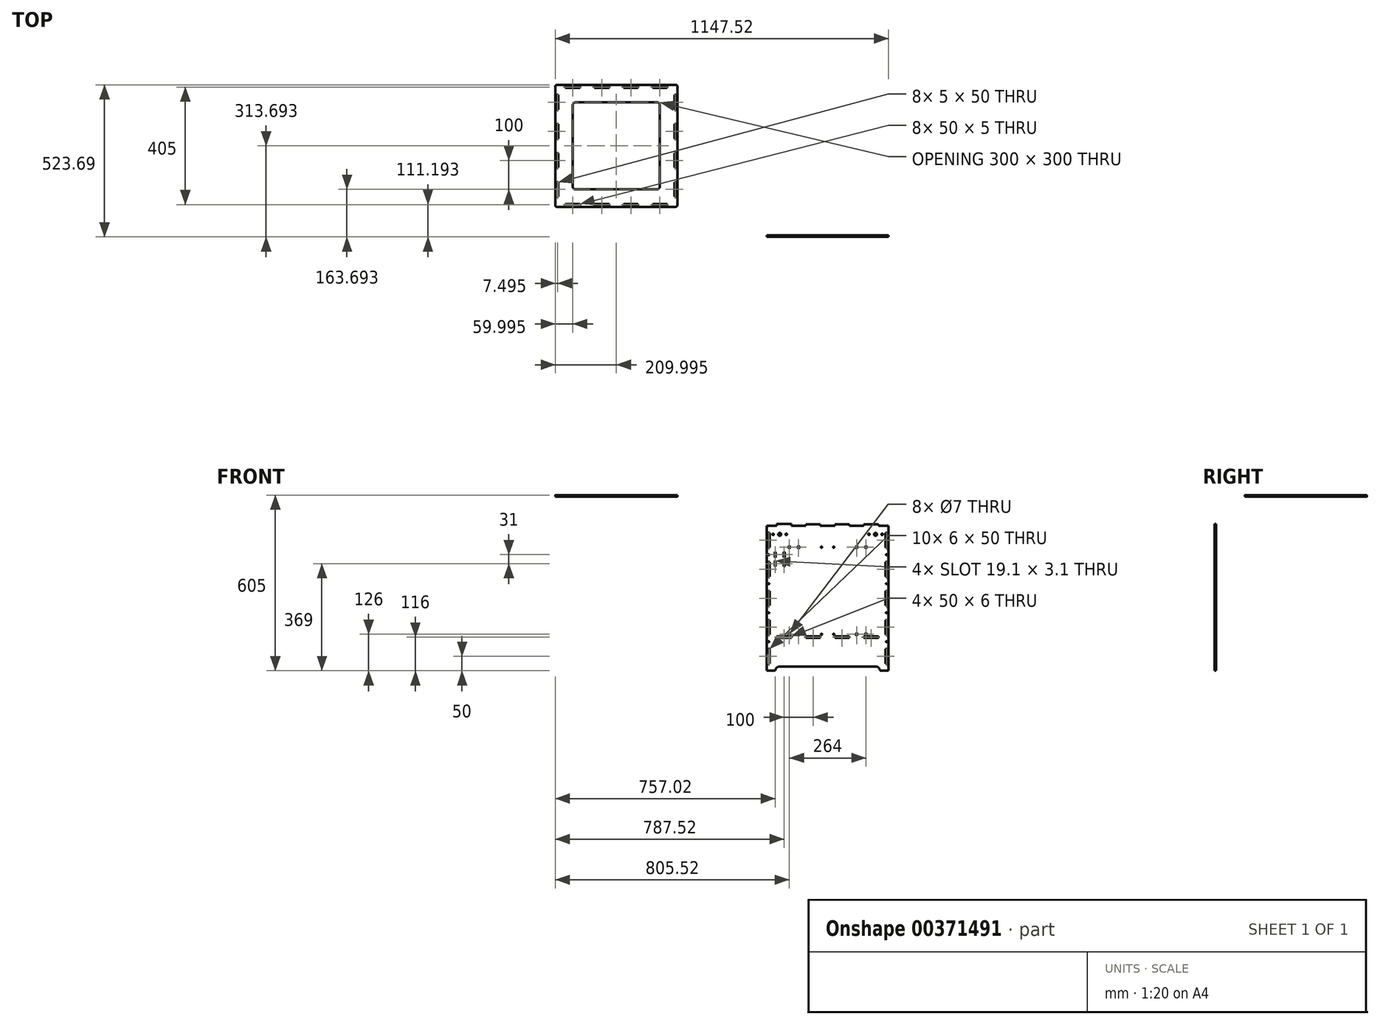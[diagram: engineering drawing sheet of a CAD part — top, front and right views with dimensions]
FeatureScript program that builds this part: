
annotation { "Feature Type Name" : "Feature", "Feature Type Description" : "" }
export const myFeature = defineFeature(function(context is Context, id is Id, definition is map)
    precondition{}
    {
        {
            var Q0;
            Q0=qCreatedBy(makeId("Front.planeOp"),FACE);
            var sketch = newSketch(context, id + "F0", { "sketchPlane" : qUnion([Q0])});
            skLineSegment(sketch, "E0.bottom", {"start": v(0, 0) * mm, "end": v(30, 0) * mm});
            skLineSegment(sketch, "E0.left", {"start": v(0, 0) * mm, "end": v(0, 500) * mm});
            skLineSegment(sketch, "E0.right", {"start": v(420, 0) * mm, "end": v(420, 500) * mm});
            skCircle(sketch, "E1", {"center": v(22.5, 470) * mm, "radius": 2.6 * mm});
            skCircle(sketch, "E2", {"center": v(67.5, 470) * mm, "radius": 2.6 * mm});
            skCircle(sketch, "E3", {"center": v(352.5, 470) * mm, "radius": 2.6 * mm});
            skCircle(sketch, "E4", {"center": v(397.5, 470) * mm, "radius": 2.6 * mm});
            skPoint(sketch, "E5.endSnap0", {"position": v(210, 0) * mm});
            skPoint(sketch, "E6.orphan", {"position": v(135, 0) * mm});
            skPoint(sketch, "E7.orphan", {"position": v(285, 0) * mm});
            skPoint(sketch, "E8", {"position": v(30, 0) * mm});
            skPoint(sketch, "E9", {"position": v(390, 0) * mm});
            skPoint(sketch, "E10", {"position": v(45, 0) * mm});
            skPoint(sketch, "E11", {"position": v(375, 0) * mm});
            skLineSegment(sketch, "E12.trimOffspring", {"start": v(390, 0) * mm, "end": v(420, 0) * mm});
            skLineSegment(sketch, "E13", {"start": v(375, 15) * mm, "end": v(45, 15) * mm});
            skArc(sketch, "E14", {"start": v(390, 0) * mm, "mid": v(385.6, 10.6) * mm, "end": v(375, 15) * mm});
            skArc(sketch, "E15", {"start": v(45, 15) * mm, "mid": v(34.4, 10.6) * mm, "end": v(30, 0) * mm});
            skCircle(sketch, "E16", {"center": v(45, 470) * mm, "radius": 5 * mm});
            skCircle(sketch, "E17", {"center": v(375, 470) * mm, "radius": 5 * mm});
            skCircle(sketch, "E18", {"center": v(231, 126) * mm, "radius": 2.1 * mm});
            skCircle(sketch, "E19", {"center": v(189, 126) * mm, "radius": 2.1 * mm});
            skCircle(sketch, "E20", {"center": v(231, 426) * mm, "radius": 2.1 * mm});
            skCircle(sketch, "E21", {"center": v(189, 426) * mm, "radius": 2.1 * mm});
            skCircle(sketch, "E22", {"center": v(342, 126) * mm, "radius": 3.5 * mm});
            skCircle(sketch, "E23", {"center": v(310, 126) * mm, "radius": 3.5 * mm});
            skCircle(sketch, "E24", {"center": v(342, 426) * mm, "radius": 3.5 * mm});
            skCircle(sketch, "E25", {"center": v(310, 426) * mm, "radius": 3.5 * mm});
            skCircle(sketch, "E26", {"center": v(110, 126) * mm, "radius": 3.5 * mm});
            skCircle(sketch, "E27", {"center": v(78, 126) * mm, "radius": 3.5 * mm});
            skCircle(sketch, "E28", {"center": v(110, 426) * mm, "radius": 3.5 * mm});
            skCircle(sketch, "E29", {"center": v(78, 426) * mm, "radius": 3.5 * mm});
            skLineSegment(sketch, "E30", {"start": v(31.05, 408) * mm, "end": v(31.05, 392) * mm});
            skLineSegment(sketch, "E31", {"start": v(27.95, 392) * mm, "end": v(27.95, 408) * mm});
            skArc(sketch, "E32", {"start": v(31.05, 408) * mm, "mid": v(29.5, 409.55) * mm, "end": v(27.95, 408) * mm});
            skArc(sketch, "E33", {"start": v(27.95, 392) * mm, "mid": v(29.5, 390.45) * mm, "end": v(31.05, 392) * mm});
            skPoint(sketch, "E34.center.orphan", {"position": v(29.5, 400) * mm});
            skPoint(sketch, "E35", {"position": v(60.5, 400) * mm});
            skPoint(sketch, "E36", {"position": v(60.5, 369) * mm});
            skPoint(sketch, "E37", {"position": v(29.5, 369) * mm});
            skLineSegment(sketch, "E38", {"start": v(31.05, 377) * mm, "end": v(31.05, 361) * mm});
            skLineSegment(sketch, "E39", {"start": v(27.95, 361) * mm, "end": v(27.95, 377) * mm});
            skArc(sketch, "E40", {"start": v(31.05, 377) * mm, "mid": v(29.5, 378.55) * mm, "end": v(27.95, 377) * mm});
            skArc(sketch, "E41", {"start": v(27.95, 361) * mm, "mid": v(29.5, 359.45) * mm, "end": v(31.05, 361) * mm});
            skLineSegment(sketch, "E42", {"start": v(62.05, 377) * mm, "end": v(62.05, 361) * mm});
            skLineSegment(sketch, "E43", {"start": v(58.95, 361) * mm, "end": v(58.95, 377) * mm});
            skArc(sketch, "E44", {"start": v(62.05, 377) * mm, "mid": v(60.5, 378.55) * mm, "end": v(58.95, 377) * mm});
            skArc(sketch, "E45", {"start": v(58.95, 361) * mm, "mid": v(60.5, 359.45) * mm, "end": v(62.05, 361) * mm});
            skLineSegment(sketch, "E46", {"start": v(62.05, 408) * mm, "end": v(62.05, 392) * mm});
            skLineSegment(sketch, "E47", {"start": v(58.95, 392) * mm, "end": v(58.95, 408) * mm});
            skArc(sketch, "E48", {"start": v(62.05, 408) * mm, "mid": v(60.5, 409.55) * mm, "end": v(58.95, 408) * mm});
            skArc(sketch, "E49", {"start": v(58.95, 392) * mm, "mid": v(60.5, 390.45) * mm, "end": v(62.05, 392) * mm});
            skLineSegment(sketch, "E50.bottom", {"start": v(4.5, 475) * mm, "end": v(10.5, 475) * mm});
            skLineSegment(sketch, "E50.top", {"start": v(4.5, 425) * mm, "end": v(10.5, 425) * mm});
            skLineSegment(sketch, "E50.left", {"start": v(4.5, 475) * mm, "end": v(4.5, 425) * mm});
            skLineSegment(sketch, "E50.right", {"start": v(10.5, 475) * mm, "end": v(10.5, 425) * mm});
            skLineSegment(sketch, "E51.0.1.0", {"start": v(4.5, 375) * mm, "end": v(4.5, 325) * mm});
            skLineSegment(sketch, "E51.0.1.1", {"start": v(4.5, 375) * mm, "end": v(10.5, 375) * mm});
            skLineSegment(sketch, "E51.0.1.2", {"start": v(10.5, 375) * mm, "end": v(10.5, 325) * mm});
            skLineSegment(sketch, "E51.0.1.3", {"start": v(4.5, 325) * mm, "end": v(10.5, 325) * mm});
            skLineSegment(sketch, "E51.0.2.0", {"start": v(4.5, 275) * mm, "end": v(4.5, 225) * mm});
            skLineSegment(sketch, "E51.0.2.1", {"start": v(4.5, 275) * mm, "end": v(10.5, 275) * mm});
            skLineSegment(sketch, "E51.0.2.2", {"start": v(10.5, 275) * mm, "end": v(10.5, 225) * mm});
            skLineSegment(sketch, "E51.0.2.3", {"start": v(4.5, 225) * mm, "end": v(10.5, 225) * mm});
            skLineSegment(sketch, "E51.0.3.0", {"start": v(4.5, 175) * mm, "end": v(4.5, 125) * mm});
            skLineSegment(sketch, "E51.0.3.1", {"start": v(4.5, 175) * mm, "end": v(10.5, 175) * mm});
            skLineSegment(sketch, "E51.0.3.2", {"start": v(10.5, 175) * mm, "end": v(10.5, 125) * mm});
            skLineSegment(sketch, "E51.0.3.3", {"start": v(4.5, 125) * mm, "end": v(10.5, 125) * mm});
            skLineSegment(sketch, "E51.0.4.0", {"start": v(4.5, 75) * mm, "end": v(4.5, 25) * mm});
            skLineSegment(sketch, "E51.0.4.1", {"start": v(4.5, 75) * mm, "end": v(10.5, 75) * mm});
            skLineSegment(sketch, "E51.0.4.2", {"start": v(10.5, 75) * mm, "end": v(10.5, 25) * mm});
            skLineSegment(sketch, "E51.0.4.3", {"start": v(4.5, 25) * mm, "end": v(10.5, 25) * mm});
            skLineSegment(sketch, "E51.1.0.0", {"start": v(409.5, 475) * mm, "end": v(409.5, 425) * mm});
            skLineSegment(sketch, "E51.1.0.1", {"start": v(409.5, 475) * mm, "end": v(415.5, 475) * mm});
            skLineSegment(sketch, "E51.1.0.2", {"start": v(415.5, 475) * mm, "end": v(415.5, 425) * mm});
            skLineSegment(sketch, "E51.1.0.3", {"start": v(409.5, 425) * mm, "end": v(415.5, 425) * mm});
            skLineSegment(sketch, "E51.1.1.0", {"start": v(409.5, 375) * mm, "end": v(409.5, 325) * mm});
            skLineSegment(sketch, "E51.1.1.1", {"start": v(409.5, 375) * mm, "end": v(415.5, 375) * mm});
            skLineSegment(sketch, "E51.1.1.2", {"start": v(415.5, 375) * mm, "end": v(415.5, 325) * mm});
            skLineSegment(sketch, "E51.1.1.3", {"start": v(409.5, 325) * mm, "end": v(415.5, 325) * mm});
            skLineSegment(sketch, "E51.1.2.0", {"start": v(409.5, 275) * mm, "end": v(409.5, 225) * mm});
            skLineSegment(sketch, "E51.1.2.1", {"start": v(409.5, 275) * mm, "end": v(415.5, 275) * mm});
            skLineSegment(sketch, "E51.1.2.2", {"start": v(415.5, 275) * mm, "end": v(415.5, 225) * mm});
            skLineSegment(sketch, "E51.1.2.3", {"start": v(409.5, 225) * mm, "end": v(415.5, 225) * mm});
            skLineSegment(sketch, "E51.1.3.0", {"start": v(409.5, 175) * mm, "end": v(409.5, 125) * mm});
            skLineSegment(sketch, "E51.1.3.1", {"start": v(409.5, 175) * mm, "end": v(415.5, 175) * mm});
            skLineSegment(sketch, "E51.1.3.2", {"start": v(415.5, 175) * mm, "end": v(415.5, 125) * mm});
            skLineSegment(sketch, "E51.1.3.3", {"start": v(409.5, 125) * mm, "end": v(415.5, 125) * mm});
            skLineSegment(sketch, "E51.1.4.0", {"start": v(409.5, 75) * mm, "end": v(409.5, 25) * mm});
            skLineSegment(sketch, "E51.1.4.1", {"start": v(409.5, 75) * mm, "end": v(415.5, 75) * mm});
            skLineSegment(sketch, "E51.1.4.2", {"start": v(415.5, 75) * mm, "end": v(415.5, 25) * mm});
            skLineSegment(sketch, "E51.1.4.3", {"start": v(409.5, 25) * mm, "end": v(415.5, 25) * mm});
            skLineSegment(sketch, "E51.direction1", {"start": v(4.5, 425) * mm, "end": v(409.5, 425) * mm, "construction": true});
            skLineSegment(sketch, "E51.direction2", {"start": v(4.5, 425) * mm, "end": v(4.5, 325) * mm, "construction": true});
            skLineSegment(sketch, "E52.bottom", {"start": v(35, 119) * mm, "end": v(85, 119) * mm});
            skLineSegment(sketch, "E52.top", {"start": v(35, 113) * mm, "end": v(85, 113) * mm});
            skLineSegment(sketch, "E52.left", {"start": v(35, 119) * mm, "end": v(35, 113) * mm});
            skLineSegment(sketch, "E52.right", {"start": v(85, 119) * mm, "end": v(85, 113) * mm});
            skLineSegment(sketch, "E53.1.0.0", {"start": v(135, 119) * mm, "end": v(185, 119) * mm});
            skLineSegment(sketch, "E53.1.0.1", {"start": v(135, 113) * mm, "end": v(185, 113) * mm});
            skLineSegment(sketch, "E53.1.0.2", {"start": v(185, 119) * mm, "end": v(185, 113) * mm});
            skLineSegment(sketch, "E53.1.0.3", {"start": v(135, 119) * mm, "end": v(135, 113) * mm});
            skLineSegment(sketch, "E53.2.0.0", {"start": v(235, 119) * mm, "end": v(285, 119) * mm});
            skLineSegment(sketch, "E53.2.0.1", {"start": v(235, 113) * mm, "end": v(285, 113) * mm});
            skLineSegment(sketch, "E53.2.0.2", {"start": v(285, 119) * mm, "end": v(285, 113) * mm});
            skLineSegment(sketch, "E53.2.0.3", {"start": v(235, 119) * mm, "end": v(235, 113) * mm});
            skLineSegment(sketch, "E53.3.0.0", {"start": v(335, 119) * mm, "end": v(385, 119) * mm});
            skLineSegment(sketch, "E53.3.0.1", {"start": v(335, 113) * mm, "end": v(385, 113) * mm});
            skLineSegment(sketch, "E53.3.0.2", {"start": v(385, 119) * mm, "end": v(385, 113) * mm});
            skLineSegment(sketch, "E53.3.0.3", {"start": v(335, 119) * mm, "end": v(335, 113) * mm});
            skLineSegment(sketch, "E53.direction1", {"start": v(35, 119) * mm, "end": v(135, 119) * mm, "construction": true});
            skLineSegment(sketch, "E53.direction2", {"start": v(35, 119) * mm, "end": v(35, 119) * mm});
            skLineSegment(sketch, "E54", {"start": v(35, 500) * mm, "end": v(35, 506) * mm});
            skLineSegment(sketch, "E55", {"start": v(35, 506) * mm, "end": v(85, 506) * mm});
            skLineSegment(sketch, "E56", {"start": v(85, 506) * mm, "end": v(85, 500) * mm});
            skLineSegment(sketch, "E57.1.0.0", {"start": v(135, 500) * mm, "end": v(135, 505) * mm});
            skLineSegment(sketch, "E57.1.0.1", {"start": v(135, 505) * mm, "end": v(185, 505) * mm});
            skLineSegment(sketch, "E57.1.0.2", {"start": v(185, 505) * mm, "end": v(185, 500) * mm});
            skLineSegment(sketch, "E57.2.0.0", {"start": v(235, 500) * mm, "end": v(235, 505) * mm});
            skLineSegment(sketch, "E57.2.0.1", {"start": v(235, 505) * mm, "end": v(285, 505) * mm});
            skLineSegment(sketch, "E57.2.0.2", {"start": v(285, 505) * mm, "end": v(285, 500) * mm});
            skLineSegment(sketch, "E57.3.0.0", {"start": v(335, 500) * mm, "end": v(335, 505) * mm});
            skLineSegment(sketch, "E57.3.0.1", {"start": v(335, 505) * mm, "end": v(385, 505) * mm});
            skLineSegment(sketch, "E57.3.0.2", {"start": v(385, 505) * mm, "end": v(385, 500) * mm});
            skLineSegment(sketch, "E58.trimOffspring", {"start": v(185, 500) * mm, "end": v(235, 500) * mm});
            skLineSegment(sketch, "E59.trimOffspring", {"start": v(285, 500) * mm, "end": v(335, 500) * mm});
            skLineSegment(sketch, "E60.trimOffspring", {"start": v(385, 500) * mm, "end": v(420, 500) * mm});
            skLineSegment(sketch, "E61.trimOffspring", {"start": v(85, 500) * mm, "end": v(135, 500) * mm});
            skLineSegment(sketch, "E62", {"start": v(0, 500) * mm, "end": v(35, 500) * mm});
            skCircle(sketch, "E63", {"center": v(412.5, 400) * mm, "radius": 1.55 * mm});
            skPoint(sketch, "E63.centerSnap0", {"position": v(412.5, 425) * mm});
            skCircle(sketch, "E64.0.1.0", {"center": v(412.5, 300) * mm, "radius": 1.55 * mm});
            skCircle(sketch, "E64.0.2.0", {"center": v(412.5, 200) * mm, "radius": 1.55 * mm});
            skCircle(sketch, "E64.0.3.0", {"center": v(412.5, 100) * mm, "radius": 1.55 * mm});
            skCircle(sketch, "E64.1.0.0", {"center": v(7.5, 400) * mm, "radius": 1.55 * mm});
            skCircle(sketch, "E64.1.1.0", {"center": v(7.5, 300) * mm, "radius": 1.55 * mm});
            skCircle(sketch, "E64.1.2.0", {"center": v(7.5, 200) * mm, "radius": 1.55 * mm});
            skCircle(sketch, "E64.1.3.0", {"center": v(7.5, 100) * mm, "radius": 1.55 * mm});
            skLineSegment(sketch, "E64.direction1", {"start": v(412.5, 400) * mm, "end": v(7.5, 400) * mm, "construction": true});
            skLineSegment(sketch, "E64.direction2", {"start": v(412.5, 400) * mm, "end": v(412.5, 300) * mm, "construction": true});
            skSolve(sketch);
        }
        {
            var Q0;
            Q0=qCreatedBy(makeId("Top.planeOp"),FACE);
            var sketch = newSketch(context, id + "F1", { "sketchPlane" : qUnion([Q0])});
            skLineSegment(sketch, "E65.left", {"start": v(0, 113.73) * mm, "end": v(0, 116.73) * mm});
            skLineSegment(sketch, "E65.right", {"start": v(398, 113.73) * mm, "end": v(398, 511.44) * mm});
            skCircle(sketch, "E66", {"center": v(80, 312.44) * mm, "radius": 70 * mm});
            skLineSegment(sketch, "E67.bottom", {"start": v(0, 122.73) * mm, "end": v(-7, 122.73) * mm});
            skLineSegment(sketch, "E67.top", {"start": v(0, 116.73) * mm, "end": v(-7, 116.73) * mm});
            skLineSegment(sketch, "E67.left", {"start": v(0, 122.73) * mm, "end": v(0, 116.73) * mm});
            skLineSegment(sketch, "E67.right", {"start": v(-7, 122.73) * mm, "end": v(-7, 116.73) * mm});
            skLineSegment(sketch, "E68.trimOffspring", {"start": v(0, 122.73) * mm, "end": v(0, 511.44) * mm});
            skLineSegment(sketch, "E69", {"start": v(0, 113.73) * mm, "end": v(398, 113.73) * mm});
            skLineSegment(sketch, "E70", {"start": v(0, 511.44) * mm, "end": v(398, 511.44) * mm});
            skLineSegment(sketch, "E71.1.0.0", {"start": v(405, 122.73) * mm, "end": v(398, 122.73) * mm});
            skLineSegment(sketch, "E71.1.0.1", {"start": v(405, 122.73) * mm, "end": v(405, 116.73) * mm});
            skLineSegment(sketch, "E71.1.0.2", {"start": v(405, 116.73) * mm, "end": v(398, 116.73) * mm});
            skLineSegment(sketch, "E71.direction1", {"start": v(-7, 116.73) * mm, "end": v(398, 116.73) * mm, "construction": true});
            skSolve(sketch);
        }
        {
            var Q0;
            Q0=qCreatedBy(makeId("Front.planeOp"),FACE);
            cPlane(context, id + "F2", {"entities" : qUnion([Q0]), "cplaneType" : CPlaneType.OFFSET, "offset" : 700 * mm, "oppositeDirection" : true, "width" : 150 * mm, "height" : 150 * mm});
        }
        {
            var Q0;
            Q0=qCreatedBy(makeId("Right.planeOp"),FACE);
            cPlane(context, id + "F3", {"entities" : qUnion([Q0]), "cplaneType" : CPlaneType.OFFSET, "offset" : 500 * mm, "width" : 150 * mm, "height" : 150 * mm});
        }
        {
            var Q0;
            Q0=qCreatedBy(makeId("Top.planeOp"),FACE);
            cPlane(context, id + "F4", {"entities" : qUnion([Q0]), "cplaneType" : CPlaneType.OFFSET, "offset" : 600 * mm, "width" : 150 * mm, "height" : 150 * mm});
        }
        {
            var Q0;
            Q0=qCreatedBy(id+"F3.planeOp",FACE);
            var sketch = newSketch(context, id + "F5", { "sketchPlane" : qUnion([Q0])});
            skLineSegment(sketch, "E72.bottom", {"start": v(77.92, 0) * mm, "end": v(107.92, 0) * mm});
            skLineSegment(sketch, "E72.top", {"start": v(77.92, 500) * mm, "end": v(477.92, 500) * mm});
            skLineSegment(sketch, "E72.left", {"start": v(77.92, 0) * mm, "end": v(77.92, 500) * mm});
            skLineSegment(sketch, "E72.right", {"start": v(477.92, 0) * mm, "end": v(477.92, 500) * mm});
            skPoint(sketch, "E73", {"position": v(107.92, 0) * mm});
            skPoint(sketch, "E74", {"position": v(447.92, 0) * mm});
            skPoint(sketch, "E75", {"position": v(122.92, 0) * mm});
            skPoint(sketch, "E76", {"position": v(432.92, 0) * mm});
            skLineSegment(sketch, "E77.trimOffspring", {"start": v(447.92, 0) * mm, "end": v(477.92, 0) * mm});
            skLineSegment(sketch, "E78.bottom", {"start": v(152.92, 130) * mm, "end": v(452.92, 130) * mm});
            skLineSegment(sketch, "E78.top", {"start": v(152.92, 430) * mm, "end": v(452.92, 430) * mm});
            skLineSegment(sketch, "E78.left", {"start": v(152.92, 130) * mm, "end": v(152.92, 430) * mm});
            skLineSegment(sketch, "E78.right", {"start": v(452.92, 130) * mm, "end": v(452.92, 430) * mm});
            skLineSegment(sketch, "E79", {"start": v(122.92, 15) * mm, "end": v(432.92, 15) * mm});
            skArc(sketch, "E80", {"start": v(122.92, 15) * mm, "mid": v(112.32, 10.6) * mm, "end": v(107.92, 0) * mm});
            skArc(sketch, "E81", {"start": v(447.92, 0) * mm, "mid": v(443.53, 10.6) * mm, "end": v(432.92, 15) * mm});
            skLineSegment(sketch, "E82.bottom", {"start": v(102.92, 120) * mm, "end": v(152.92, 120) * mm});
            skLineSegment(sketch, "E82.top", {"start": v(102.92, 114) * mm, "end": v(152.92, 114) * mm});
            skLineSegment(sketch, "E82.left", {"start": v(102.92, 120) * mm, "end": v(102.92, 114) * mm});
            skLineSegment(sketch, "E82.right", {"start": v(152.92, 120) * mm, "end": v(152.92, 114) * mm});
            skLineSegment(sketch, "E83.1.0.0", {"start": v(252.92, 120) * mm, "end": v(252.92, 114) * mm});
            skLineSegment(sketch, "E83.1.0.1", {"start": v(202.92, 120) * mm, "end": v(252.92, 120) * mm});
            skLineSegment(sketch, "E83.1.0.2", {"start": v(202.92, 114) * mm, "end": v(252.92, 114) * mm});
            skLineSegment(sketch, "E83.1.0.3", {"start": v(202.92, 120) * mm, "end": v(202.92, 114) * mm});
            skLineSegment(sketch, "E83.2.0.0", {"start": v(352.92, 120) * mm, "end": v(352.92, 114) * mm});
            skLineSegment(sketch, "E83.2.0.1", {"start": v(302.92, 120) * mm, "end": v(352.92, 120) * mm});
            skLineSegment(sketch, "E83.2.0.2", {"start": v(302.92, 114) * mm, "end": v(352.92, 114) * mm});
            skLineSegment(sketch, "E83.2.0.3", {"start": v(302.92, 120) * mm, "end": v(302.92, 114) * mm});
            skLineSegment(sketch, "E83.3.0.0", {"start": v(452.92, 120) * mm, "end": v(452.92, 114) * mm});
            skLineSegment(sketch, "E83.3.0.1", {"start": v(402.92, 120) * mm, "end": v(452.92, 120) * mm});
            skLineSegment(sketch, "E83.3.0.2", {"start": v(402.92, 114) * mm, "end": v(452.92, 114) * mm});
            skLineSegment(sketch, "E83.3.0.3", {"start": v(402.92, 120) * mm, "end": v(402.92, 114) * mm});
            skLineSegment(sketch, "E83.direction1", {"start": v(102.92, 114) * mm, "end": v(202.92, 114) * mm, "construction": true});
            skLineSegment(sketch, "E84", {"start": v(77.92, 475) * mm, "end": v(71.92, 475) * mm});
            skLineSegment(sketch, "E85", {"start": v(71.92, 475) * mm, "end": v(71.92, 425) * mm});
            skLineSegment(sketch, "E86", {"start": v(71.92, 425) * mm, "end": v(77.92, 425) * mm});
            skLineSegment(sketch, "E87.0.1.0", {"start": v(77.92, 375) * mm, "end": v(71.92, 375) * mm});
            skLineSegment(sketch, "E87.0.1.1", {"start": v(71.92, 375) * mm, "end": v(71.92, 325) * mm});
            skLineSegment(sketch, "E87.0.1.2", {"start": v(71.92, 325) * mm, "end": v(77.92, 325) * mm});
            skLineSegment(sketch, "E87.0.2.0", {"start": v(77.92, 275) * mm, "end": v(71.92, 275) * mm});
            skLineSegment(sketch, "E87.0.2.1", {"start": v(71.92, 275) * mm, "end": v(71.92, 225) * mm});
            skLineSegment(sketch, "E87.0.2.2", {"start": v(71.92, 225) * mm, "end": v(77.92, 225) * mm});
            skLineSegment(sketch, "E87.0.3.0", {"start": v(77.92, 175) * mm, "end": v(71.92, 175) * mm});
            skLineSegment(sketch, "E87.0.3.1", {"start": v(71.92, 175) * mm, "end": v(71.92, 125) * mm});
            skLineSegment(sketch, "E87.0.3.2", {"start": v(71.92, 125) * mm, "end": v(77.92, 125) * mm});
            skLineSegment(sketch, "E87.0.4.0", {"start": v(77.92, 75) * mm, "end": v(71.92, 75) * mm});
            skLineSegment(sketch, "E87.0.4.1", {"start": v(71.92, 75) * mm, "end": v(71.92, 25) * mm});
            skLineSegment(sketch, "E87.0.4.2", {"start": v(71.92, 25) * mm, "end": v(77.92, 25) * mm});
            skLineSegment(sketch, "E87.direction1", {"start": v(71.92, 475) * mm, "end": v(92.92, 475) * mm, "construction": true});
            skLineSegment(sketch, "E87.direction2", {"start": v(71.92, 475) * mm, "end": v(71.92, 375) * mm, "construction": true});
            skLineSegment(sketch, "E88.bottom", {"start": v(570.54, 14.2) * mm, "end": v(576.54, 14.2) * mm});
            skLineSegment(sketch, "E88.top", {"start": v(570.54, 20.2) * mm, "end": v(576.54, 20.2) * mm});
            skLineSegment(sketch, "E88.left", {"start": v(570.54, 14.2) * mm, "end": v(570.54, 20.2) * mm});
            skLineSegment(sketch, "E88.right", {"start": v(576.54, 14.2) * mm, "end": v(576.54, 20.2) * mm});
            skCircle(sketch, "E89", {"center": v(573.54, 17.2) * mm, "radius": 4.24 * mm});
            skPoint(sketch, "E89.centerSnap0", {"position": v(576.54, 17.2) * mm});
            skPoint(sketch, "E89.centerSnap1", {"position": v(573.54, 20.2) * mm});
            skCircle(sketch, "E90", {"center": v(87.12, 21) * mm, "radius": 4.2 * mm});
            skLineSegment(sketch, "E91.0.1.0", {"start": v(477.92, 425) * mm, "end": v(483.92, 425) * mm});
            skLineSegment(sketch, "E91.0.1.1", {"start": v(483.92, 425) * mm, "end": v(483.92, 475) * mm});
            skLineSegment(sketch, "E91.0.1.2", {"start": v(483.92, 475) * mm, "end": v(477.92, 475) * mm});
            skLineSegment(sketch, "E92.0.1.0", {"start": v(483.92, 375) * mm, "end": v(477.92, 375) * mm});
            skLineSegment(sketch, "E92.0.1.1", {"start": v(483.92, 325) * mm, "end": v(483.92, 375) * mm});
            skLineSegment(sketch, "E92.0.1.2", {"start": v(477.92, 325) * mm, "end": v(483.92, 325) * mm});
            skLineSegment(sketch, "E92.0.2.0", {"start": v(483.92, 275) * mm, "end": v(477.92, 275) * mm});
            skLineSegment(sketch, "E92.0.2.1", {"start": v(483.92, 225) * mm, "end": v(483.92, 275) * mm});
            skLineSegment(sketch, "E92.0.2.2", {"start": v(477.92, 225) * mm, "end": v(483.92, 225) * mm});
            skLineSegment(sketch, "E92.0.3.0", {"start": v(483.92, 175) * mm, "end": v(477.92, 175) * mm});
            skLineSegment(sketch, "E92.0.3.1", {"start": v(483.92, 125) * mm, "end": v(483.92, 175) * mm});
            skLineSegment(sketch, "E92.0.3.2", {"start": v(477.92, 125) * mm, "end": v(483.92, 125) * mm});
            skLineSegment(sketch, "E92.0.4.0", {"start": v(483.92, 75) * mm, "end": v(477.92, 75) * mm});
            skLineSegment(sketch, "E92.0.4.1", {"start": v(483.92, 25) * mm, "end": v(483.92, 75) * mm});
            skLineSegment(sketch, "E92.0.4.2", {"start": v(477.92, 25) * mm, "end": v(483.92, 25) * mm});
            skLineSegment(sketch, "E92.direction1", {"start": v(477.92, 425) * mm, "end": v(502.92, 425) * mm, "construction": true});
            skLineSegment(sketch, "E92.direction2", {"start": v(477.92, 425) * mm, "end": v(477.92, 325) * mm, "construction": true});
            skLineSegment(sketch, "E93", {"start": v(102.92, 500) * mm, "end": v(102.92, 506) * mm});
            skLineSegment(sketch, "E94", {"start": v(102.92, 506) * mm, "end": v(152.92, 506) * mm});
            skLineSegment(sketch, "E95", {"start": v(152.92, 506) * mm, "end": v(152.92, 500) * mm});
            skLineSegment(sketch, "E96.1.0.0", {"start": v(202.92, 500) * mm, "end": v(202.92, 506) * mm});
            skLineSegment(sketch, "E96.1.0.1", {"start": v(202.92, 506) * mm, "end": v(252.92, 506) * mm});
            skLineSegment(sketch, "E96.1.0.2", {"start": v(252.92, 506) * mm, "end": v(252.92, 500) * mm});
            skLineSegment(sketch, "E96.2.0.0", {"start": v(302.92, 500) * mm, "end": v(302.92, 506) * mm});
            skLineSegment(sketch, "E96.2.0.1", {"start": v(302.92, 506) * mm, "end": v(352.92, 506) * mm});
            skLineSegment(sketch, "E96.2.0.2", {"start": v(352.92, 506) * mm, "end": v(352.92, 500) * mm});
            skLineSegment(sketch, "E96.3.0.0", {"start": v(402.92, 500) * mm, "end": v(402.92, 506) * mm});
            skLineSegment(sketch, "E96.3.0.1", {"start": v(402.92, 506) * mm, "end": v(452.92, 506) * mm});
            skLineSegment(sketch, "E96.3.0.2", {"start": v(452.92, 506) * mm, "end": v(452.92, 500) * mm});
            skLineSegment(sketch, "E96.direction1", {"start": v(112.92, 500) * mm, "end": v(212.92, 500) * mm, "construction": true});
            skSolve(sketch);
        }
        {
            var Q0;
            Q0=makeQuery(id+"F0.imprint","IMPRINT",FACE,{"disambiguationData":[TD([[makeQuery(id+"F0.imprint","IMPRINT",EDGE,{"derivedFrom":sQuery(id+"F0.wireOp",EDGE,"E0.bottom")}),1.0]])]});
            extrude(context, id + "F6", {"entities" : qUnion([Q0]), "depth" : 5 * mm});
        }
        {
            var Q0;
            Q0=qCreatedBy(id+"F4.planeOp",FACE);
            var sketch = newSketch(context, id + "F7", { "sketchPlane" : qUnion([Q0])});
            skLineSegment(sketch, "E97.bottom", {"start": v(-722.52, 98.7) * mm, "end": v(-312.52, 98.7) * mm});
            skLineSegment(sketch, "E97.top", {"start": v(-722.52, 518.7) * mm, "end": v(-312.52, 518.7) * mm});
            skLineSegment(sketch, "E97.left", {"start": v(-727.52, 103.7) * mm, "end": v(-727.52, 513.7) * mm});
            skLineSegment(sketch, "E97.right", {"start": v(-307.52, 103.7) * mm, "end": v(-307.52, 513.7) * mm});
            skLineSegment(sketch, "E98.bottom", {"start": v(-657.52, 458.7) * mm, "end": v(-377.52, 458.7) * mm});
            skLineSegment(sketch, "E98.top", {"start": v(-657.52, 158.7) * mm, "end": v(-377.52, 158.7) * mm});
            skLineSegment(sketch, "E98.left", {"start": v(-667.52, 448.7) * mm, "end": v(-667.52, 168.7) * mm});
            skLineSegment(sketch, "E98.right", {"start": v(-367.52, 448.7) * mm, "end": v(-367.52, 168.7) * mm});
            skLineSegment(sketch, "E99.bottom", {"start": v(-722.52, 483.7) * mm, "end": v(-717.52, 483.7) * mm});
            skLineSegment(sketch, "E99.top", {"start": v(-722.52, 433.7) * mm, "end": v(-717.52, 433.7) * mm});
            skLineSegment(sketch, "E99.left", {"start": v(-722.52, 483.7) * mm, "end": v(-722.52, 433.7) * mm});
            skLineSegment(sketch, "E99.right", {"start": v(-717.52, 483.7) * mm, "end": v(-717.52, 433.7) * mm});
            skLineSegment(sketch, "E100.bottom", {"start": v(-692.52, 103.7) * mm, "end": v(-692.52, 108.7) * mm});
            skLineSegment(sketch, "E100.top", {"start": v(-642.52, 103.7) * mm, "end": v(-642.52, 108.7) * mm});
            skLineSegment(sketch, "E100.left", {"start": v(-692.52, 103.7) * mm, "end": v(-642.52, 103.7) * mm});
            skLineSegment(sketch, "E100.right", {"start": v(-692.52, 108.7) * mm, "end": v(-642.52, 108.7) * mm});
            skLineSegment(sketch, "E101.0.1.0", {"start": v(-692.52, 508.7) * mm, "end": v(-642.52, 508.7) * mm});
            skLineSegment(sketch, "E101.0.1.1", {"start": v(-692.52, 513.7) * mm, "end": v(-642.52, 513.7) * mm});
            skLineSegment(sketch, "E101.0.1.2", {"start": v(-642.52, 508.7) * mm, "end": v(-642.52, 513.7) * mm});
            skLineSegment(sketch, "E101.0.1.3", {"start": v(-692.52, 508.7) * mm, "end": v(-692.52, 513.7) * mm});
            skLineSegment(sketch, "E101.1.0.0", {"start": v(-592.52, 103.7) * mm, "end": v(-542.52, 103.7) * mm});
            skLineSegment(sketch, "E101.1.0.1", {"start": v(-592.52, 108.7) * mm, "end": v(-542.52, 108.7) * mm});
            skLineSegment(sketch, "E101.1.0.2", {"start": v(-542.52, 103.7) * mm, "end": v(-542.52, 108.7) * mm});
            skLineSegment(sketch, "E101.1.0.3", {"start": v(-592.52, 103.7) * mm, "end": v(-592.52, 108.7) * mm});
            skLineSegment(sketch, "E101.1.1.0", {"start": v(-592.52, 508.7) * mm, "end": v(-542.52, 508.7) * mm});
            skLineSegment(sketch, "E101.1.1.1", {"start": v(-592.52, 513.7) * mm, "end": v(-542.52, 513.7) * mm});
            skLineSegment(sketch, "E101.1.1.2", {"start": v(-542.52, 508.7) * mm, "end": v(-542.52, 513.7) * mm});
            skLineSegment(sketch, "E101.1.1.3", {"start": v(-592.52, 508.7) * mm, "end": v(-592.52, 513.7) * mm});
            skLineSegment(sketch, "E101.2.0.0", {"start": v(-492.52, 103.7) * mm, "end": v(-442.52, 103.7) * mm});
            skLineSegment(sketch, "E101.2.0.1", {"start": v(-492.52, 108.7) * mm, "end": v(-442.52, 108.7) * mm});
            skLineSegment(sketch, "E101.2.0.2", {"start": v(-442.52, 103.7) * mm, "end": v(-442.52, 108.7) * mm});
            skLineSegment(sketch, "E101.2.0.3", {"start": v(-492.52, 103.7) * mm, "end": v(-492.52, 108.7) * mm});
            skLineSegment(sketch, "E101.2.1.0", {"start": v(-492.52, 508.7) * mm, "end": v(-442.52, 508.7) * mm});
            skLineSegment(sketch, "E101.2.1.1", {"start": v(-492.52, 513.7) * mm, "end": v(-442.52, 513.7) * mm});
            skLineSegment(sketch, "E101.2.1.2", {"start": v(-442.52, 508.7) * mm, "end": v(-442.52, 513.7) * mm});
            skLineSegment(sketch, "E101.2.1.3", {"start": v(-492.52, 508.7) * mm, "end": v(-492.52, 513.7) * mm});
            skLineSegment(sketch, "E101.3.0.0", {"start": v(-392.52, 103.7) * mm, "end": v(-342.52, 103.7) * mm});
            skLineSegment(sketch, "E101.3.0.1", {"start": v(-392.52, 108.7) * mm, "end": v(-342.52, 108.7) * mm});
            skLineSegment(sketch, "E101.3.0.2", {"start": v(-342.52, 103.7) * mm, "end": v(-342.52, 108.7) * mm});
            skLineSegment(sketch, "E101.3.0.3", {"start": v(-392.52, 103.7) * mm, "end": v(-392.52, 108.7) * mm});
            skLineSegment(sketch, "E101.3.1.0", {"start": v(-392.52, 508.7) * mm, "end": v(-342.52, 508.7) * mm});
            skLineSegment(sketch, "E101.3.1.1", {"start": v(-392.52, 513.7) * mm, "end": v(-342.52, 513.7) * mm});
            skLineSegment(sketch, "E101.3.1.2", {"start": v(-342.52, 508.7) * mm, "end": v(-342.52, 513.7) * mm});
            skLineSegment(sketch, "E101.3.1.3", {"start": v(-392.52, 508.7) * mm, "end": v(-392.52, 513.7) * mm});
            skLineSegment(sketch, "E101.direction1", {"start": v(-692.52, 103.7) * mm, "end": v(-592.52, 103.7) * mm, "construction": true});
            skLineSegment(sketch, "E101.direction2", {"start": v(-692.52, 103.7) * mm, "end": v(-692.52, 508.7) * mm, "construction": true});
            skLineSegment(sketch, "E102.0.1.0", {"start": v(-722.52, 383.7) * mm, "end": v(-722.52, 333.7) * mm});
            skLineSegment(sketch, "E102.0.1.1", {"start": v(-722.52, 383.7) * mm, "end": v(-717.52, 383.7) * mm});
            skLineSegment(sketch, "E102.0.1.2", {"start": v(-717.52, 383.7) * mm, "end": v(-717.52, 333.7) * mm});
            skLineSegment(sketch, "E102.0.1.3", {"start": v(-722.52, 333.7) * mm, "end": v(-717.52, 333.7) * mm});
            skLineSegment(sketch, "E102.0.2.0", {"start": v(-722.52, 283.7) * mm, "end": v(-722.52, 233.7) * mm});
            skLineSegment(sketch, "E102.0.2.1", {"start": v(-722.52, 283.7) * mm, "end": v(-717.52, 283.7) * mm});
            skLineSegment(sketch, "E102.0.2.2", {"start": v(-717.52, 283.7) * mm, "end": v(-717.52, 233.7) * mm});
            skLineSegment(sketch, "E102.0.2.3", {"start": v(-722.52, 233.7) * mm, "end": v(-717.52, 233.7) * mm});
            skLineSegment(sketch, "E102.0.3.0", {"start": v(-722.52, 183.7) * mm, "end": v(-722.52, 133.7) * mm});
            skLineSegment(sketch, "E102.0.3.1", {"start": v(-722.52, 183.7) * mm, "end": v(-717.52, 183.7) * mm});
            skLineSegment(sketch, "E102.0.3.2", {"start": v(-717.52, 183.7) * mm, "end": v(-717.52, 133.7) * mm});
            skLineSegment(sketch, "E102.0.3.3", {"start": v(-722.52, 133.7) * mm, "end": v(-717.52, 133.7) * mm});
            skLineSegment(sketch, "E102.1.0.0", {"start": v(-317.52, 483.7) * mm, "end": v(-317.52, 433.7) * mm});
            skLineSegment(sketch, "E102.1.0.1", {"start": v(-317.52, 483.7) * mm, "end": v(-312.52, 483.7) * mm});
            skLineSegment(sketch, "E102.1.0.2", {"start": v(-312.52, 483.7) * mm, "end": v(-312.52, 433.7) * mm});
            skLineSegment(sketch, "E102.1.0.3", {"start": v(-317.52, 433.7) * mm, "end": v(-312.52, 433.7) * mm});
            skLineSegment(sketch, "E102.1.1.0", {"start": v(-317.52, 383.7) * mm, "end": v(-317.52, 333.7) * mm});
            skLineSegment(sketch, "E102.1.1.1", {"start": v(-317.52, 383.7) * mm, "end": v(-312.52, 383.7) * mm});
            skLineSegment(sketch, "E102.1.1.2", {"start": v(-312.52, 383.7) * mm, "end": v(-312.52, 333.7) * mm});
            skLineSegment(sketch, "E102.1.1.3", {"start": v(-317.52, 333.7) * mm, "end": v(-312.52, 333.7) * mm});
            skLineSegment(sketch, "E102.1.2.0", {"start": v(-317.52, 283.7) * mm, "end": v(-317.52, 233.7) * mm});
            skLineSegment(sketch, "E102.1.2.1", {"start": v(-317.52, 283.7) * mm, "end": v(-312.52, 283.7) * mm});
            skLineSegment(sketch, "E102.1.2.2", {"start": v(-312.52, 283.7) * mm, "end": v(-312.52, 233.7) * mm});
            skLineSegment(sketch, "E102.1.2.3", {"start": v(-317.52, 233.7) * mm, "end": v(-312.52, 233.7) * mm});
            skLineSegment(sketch, "E102.1.3.0", {"start": v(-317.52, 183.7) * mm, "end": v(-317.52, 133.7) * mm});
            skLineSegment(sketch, "E102.1.3.1", {"start": v(-317.52, 183.7) * mm, "end": v(-312.52, 183.7) * mm});
            skLineSegment(sketch, "E102.1.3.2", {"start": v(-312.52, 183.7) * mm, "end": v(-312.52, 133.7) * mm});
            skLineSegment(sketch, "E102.1.3.3", {"start": v(-317.52, 133.7) * mm, "end": v(-312.52, 133.7) * mm});
            skLineSegment(sketch, "E102.direction1", {"start": v(-722.52, 433.7) * mm, "end": v(-317.52, 433.7) * mm, "construction": true});
            skLineSegment(sketch, "E102.direction2", {"start": v(-722.52, 433.7) * mm, "end": v(-722.52, 333.7) * mm, "construction": true});
            skPoint(sketch, "E103.visualSharp", {"position": v(-667.52, 158.7) * mm});
            skArc(sketch, "E103.filletArc", {"start": v(-667.52, 168.7) * mm, "mid": v(-664.6, 161.62) * mm, "end": v(-657.52, 158.7) * mm});
            skPoint(sketch, "E104.visualSharp", {"position": v(-367.52, 158.7) * mm});
            skArc(sketch, "E104.filletArc", {"start": v(-377.52, 158.7) * mm, "mid": v(-370.45, 161.62) * mm, "end": v(-367.52, 168.7) * mm});
            skPoint(sketch, "E105.visualSharp", {"position": v(-367.52, 458.7) * mm});
            skArc(sketch, "E105.filletArc", {"start": v(-367.52, 448.7) * mm, "mid": v(-370.45, 455.76) * mm, "end": v(-377.52, 458.7) * mm});
            skPoint(sketch, "E106.visualSharp", {"position": v(-667.52, 458.7) * mm});
            skArc(sketch, "E106.filletArc", {"start": v(-657.52, 458.7) * mm, "mid": v(-664.6, 455.76) * mm, "end": v(-667.52, 448.7) * mm});
            skPoint(sketch, "E107.visualSharp", {"position": v(-307.52, 518.7) * mm});
            skArc(sketch, "E107.filletArc", {"start": v(-307.52, 513.7) * mm, "mid": v(-308.99, 517.23) * mm, "end": v(-312.52, 518.7) * mm});
            skPoint(sketch, "E108.visualSharp", {"position": v(-727.52, 518.7) * mm});
            skArc(sketch, "E108.filletArc", {"start": v(-722.52, 518.7) * mm, "mid": v(-726.06, 517.23) * mm, "end": v(-727.52, 513.7) * mm});
            skPoint(sketch, "E109.visualSharp", {"position": v(-727.52, 98.7) * mm});
            skArc(sketch, "E109.filletArc", {"start": v(-727.52, 103.7) * mm, "mid": v(-726.06, 100.16) * mm, "end": v(-722.52, 98.7) * mm});
            skPoint(sketch, "E110.visualSharp", {"position": v(-307.52, 98.7) * mm});
            skArc(sketch, "E110.filletArc", {"start": v(-312.52, 98.7) * mm, "mid": v(-308.99, 100.16) * mm, "end": v(-307.52, 103.7) * mm});
            skSolve(sketch);
        }
        {
            var Q0;
            Q0=makeQuery(id+"F7.imprint","IMPRINT",FACE,{"disambiguationData":[TD([[makeQuery(id+"F7.imprint","IMPRINT",EDGE,{"derivedFrom":sQuery(id+"F7.wireOp",EDGE,"E97.bottom")}),1.0]])]});
            extrude(context, id + "F8", {"entities" : qUnion([Q0]), "depth" : 5 * mm});
        }
    });
